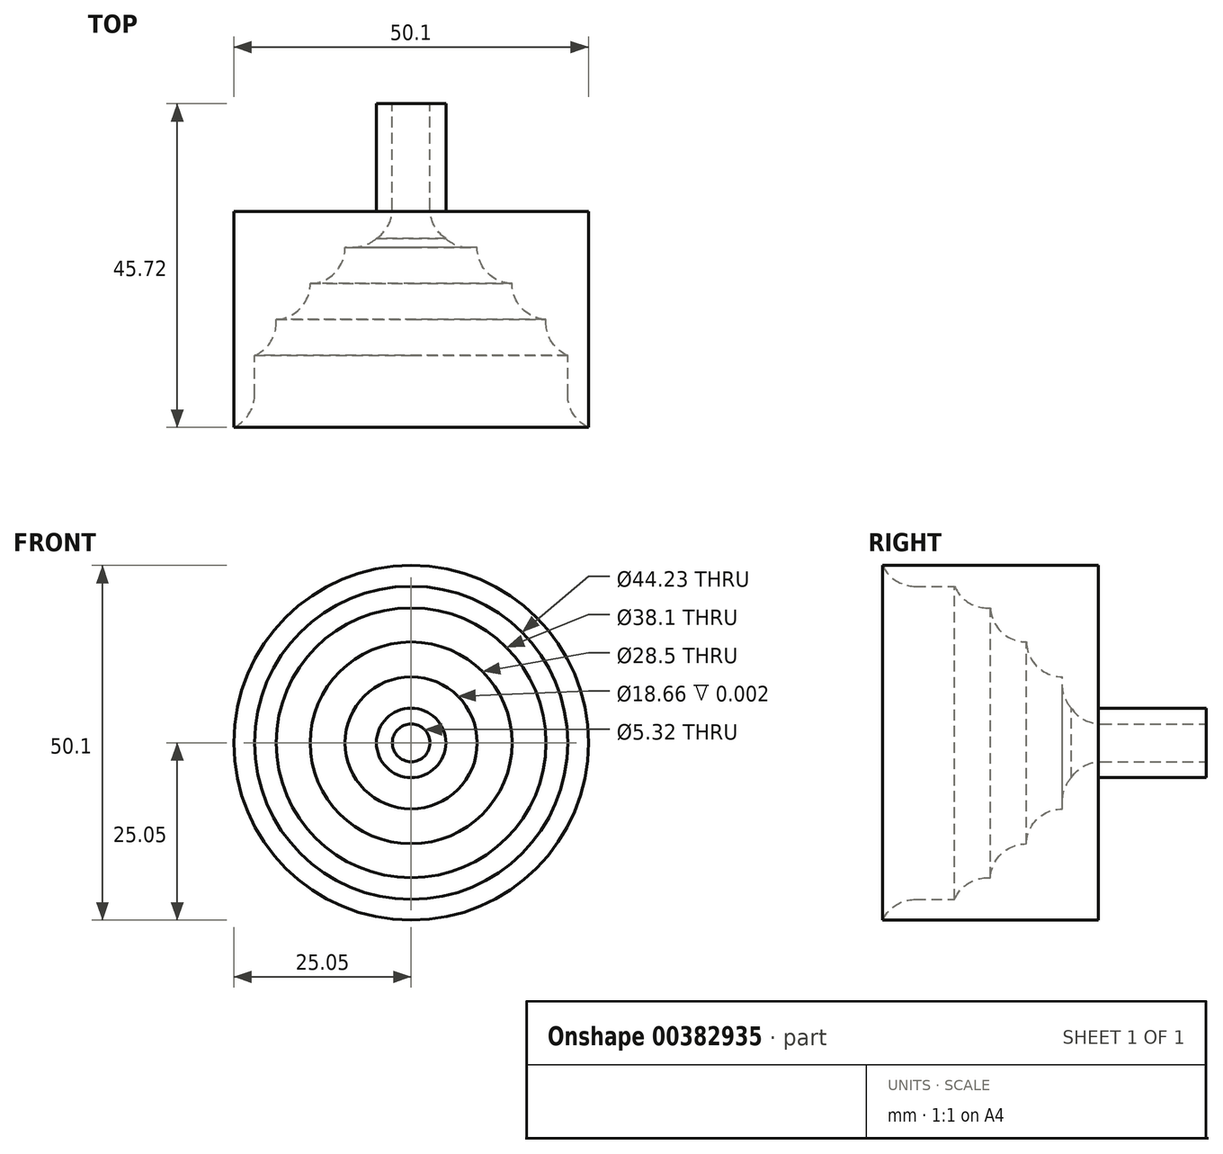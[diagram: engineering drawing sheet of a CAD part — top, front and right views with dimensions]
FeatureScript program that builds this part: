
annotation { "Feature Type Name" : "Feature", "Feature Type Description" : "" }
export const myFeature = defineFeature(function(context is Context, id is Id, definition is map)
    precondition{}
    {
        {
            var Q0;
            Q0=qCreatedBy(makeId("Front.planeOp"),FACE);
            var sketch = newSketch(context, id + "F0", { "sketchPlane" : qUnion([Q0])});
            skCircle(sketch, "E0", {"center": v(0, 0) * mm, "radius": 19.05 * mm});
            skCircle(sketch, "E1", {"center": v(0, 0) * mm, "radius": 14.25 * mm});
            skCircle(sketch, "E2", {"center": v(0, 0) * mm, "radius": 9.33 * mm});
            skCircle(sketch, "E3", {"center": v(0, 0) * mm, "radius": 4.9 * mm});
            skCircle(sketch, "E4", {"center": v(0, 0) * mm, "radius": 2.66 * mm});
            skCircle(sketch, "E5", {"center": v(0, 0) * mm, "radius": 22.12 * mm});
            skCircle(sketch, "E6", {"center": v(0, 0) * mm, "radius": 25.05 * mm});
            skSolve(sketch);
        }
        {
            var Q0;
            Q0=makeQuery(id+"F0.imprint","IMPRINT",FACE,{"disambiguationData":[TD([[makeQuery(id+"F0.imprint","IMPRINT",EDGE,{"derivedFrom":sQuery(id+"F0.wireOp",EDGE,"E5")}),-1.0]])]});
            extrude(context, id + "F1", {"entities" : qUnion([Q0]), "depth" : 30.48 * mm});
        }
        {
            var Q0;
            Q0=makeQuery(id+"F0.imprint","IMPRINT",FACE,{"disambiguationData":[TD([[makeQuery(id+"F0.imprint","IMPRINT",EDGE,{"derivedFrom":sQuery(id+"F0.wireOp",EDGE,"E0")}),-1.0]])]});
            extrude(context, id + "F2", {"entities" : qUnion([Q0]), "operationType" : NewBodyOperationType.ADD, "depth" : 20.32 * mm});
        }
        {
            var Q0;
            Q0=makeQuery(id+"F0.imprint","IMPRINT",FACE,{"disambiguationData":[TD([[makeQuery(id+"F0.imprint","IMPRINT",EDGE,{"derivedFrom":sQuery(id+"F0.wireOp",EDGE,"E0")}),1.0]])]});
            extrude(context, id + "F3", {"entities" : qUnion([Q0]), "operationType" : NewBodyOperationType.ADD, "depth" : 15.24 * mm});
        }
        {
            var Q0;
            Q0=makeQuery(id+"F0.imprint","IMPRINT",FACE,{"disambiguationData":[TD([[makeQuery(id+"F0.imprint","IMPRINT",EDGE,{"derivedFrom":sQuery(id+"F0.wireOp",EDGE,"E1")}),1.0]])]});
            extrude(context, id + "F4", {"entities" : qUnion([Q0]), "operationType" : NewBodyOperationType.ADD, "depth" : 10.16 * mm});
        }
        {
            var Q0;
            Q0=makeQuery(id+"F0.imprint","IMPRINT",FACE,{"disambiguationData":[TD([[makeQuery(id+"F0.imprint","IMPRINT",EDGE,{"derivedFrom":sQuery(id+"F0.wireOp",EDGE,"E2")}),1.0]])]});
            extrude(context, id + "F5", {"entities" : qUnion([Q0]), "operationType" : NewBodyOperationType.ADD, "depth" : 5.08 * mm});
        }
        {
            var Q0;
            Q0=makeQuery(id+"F0.imprint","IMPRINT",FACE,{"disambiguationData":[TD([[makeQuery(id+"F0.imprint","IMPRINT",EDGE,{"derivedFrom":sQuery(id+"F0.wireOp",EDGE,"E3")}),1.0]])]});
            extrude(context, id + "F6", {"entities" : qUnion([Q0]), "operationType" : NewBodyOperationType.ADD, "depth" : 3.8 * mm});
        }
        {
            var Q0;
            Q0=makeQuery(id+"F0.imprint","IMPRINT",FACE,{"disambiguationData":[TD([[makeQuery(id+"F0.imprint","IMPRINT",EDGE,{"derivedFrom":sQuery(id+"F0.wireOp",EDGE,"E3")}),1.0]])]});
            extrude(context, id + "F7", {"entities" : qUnion([Q0]), "operationType" : NewBodyOperationType.ADD, "oppositeDirection" : true, "depth" : 15.24 * mm});
        }
        {
            var Q0;
            Q0=makeQuery(id+"F1.opExtrude","CAP_EDGE",EDGE,{"disambiguationData":[OSD([sQuery(id+"F0.wireOp",EDGE,"E5")])],"isStart":false});
            var Q1;
            Q1=makeQuery(id+"F2.opExtrude","CAP_EDGE",EDGE,{"disambiguationData":[OSD([sQuery(id+"F0.wireOp",EDGE,"E0")])],"isStart":false});
            var Q2;
            Q2=makeQuery(id+"F3.opExtrude","CAP_EDGE",EDGE,{"disambiguationData":[OSD([sQuery(id+"F0.wireOp",EDGE,"E1")])],"isStart":false});
            var Q3;
            Q3=makeQuery(id+"F4.opExtrude","CAP_EDGE",EDGE,{"disambiguationData":[OSD([sQuery(id+"F0.wireOp",EDGE,"E2")])],"isStart":false});
            var Q4;
            Q4=makeQuery(id+"F5.opExtrude","CAP_EDGE",EDGE,{"disambiguationData":[OSD([sQuery(id+"F0.wireOp",EDGE,"E3")])],"isStart":false});
            var Q5;
            Q5=makeQuery(id+"F6.opExtrude","CAP_EDGE",EDGE,{"disambiguationData":[OSD([sQuery(id+"F0.wireOp",EDGE,"E4")])],"isStart":false});
            fillet(context, id + "F8", {"entities" : qUnion([Q0, Q1, Q2, Q3, Q4, Q5]), "radius" : 5.08 * mm, "tangentPropagation" : true, "allowEdgeOverflow" : false});
        }
    });
